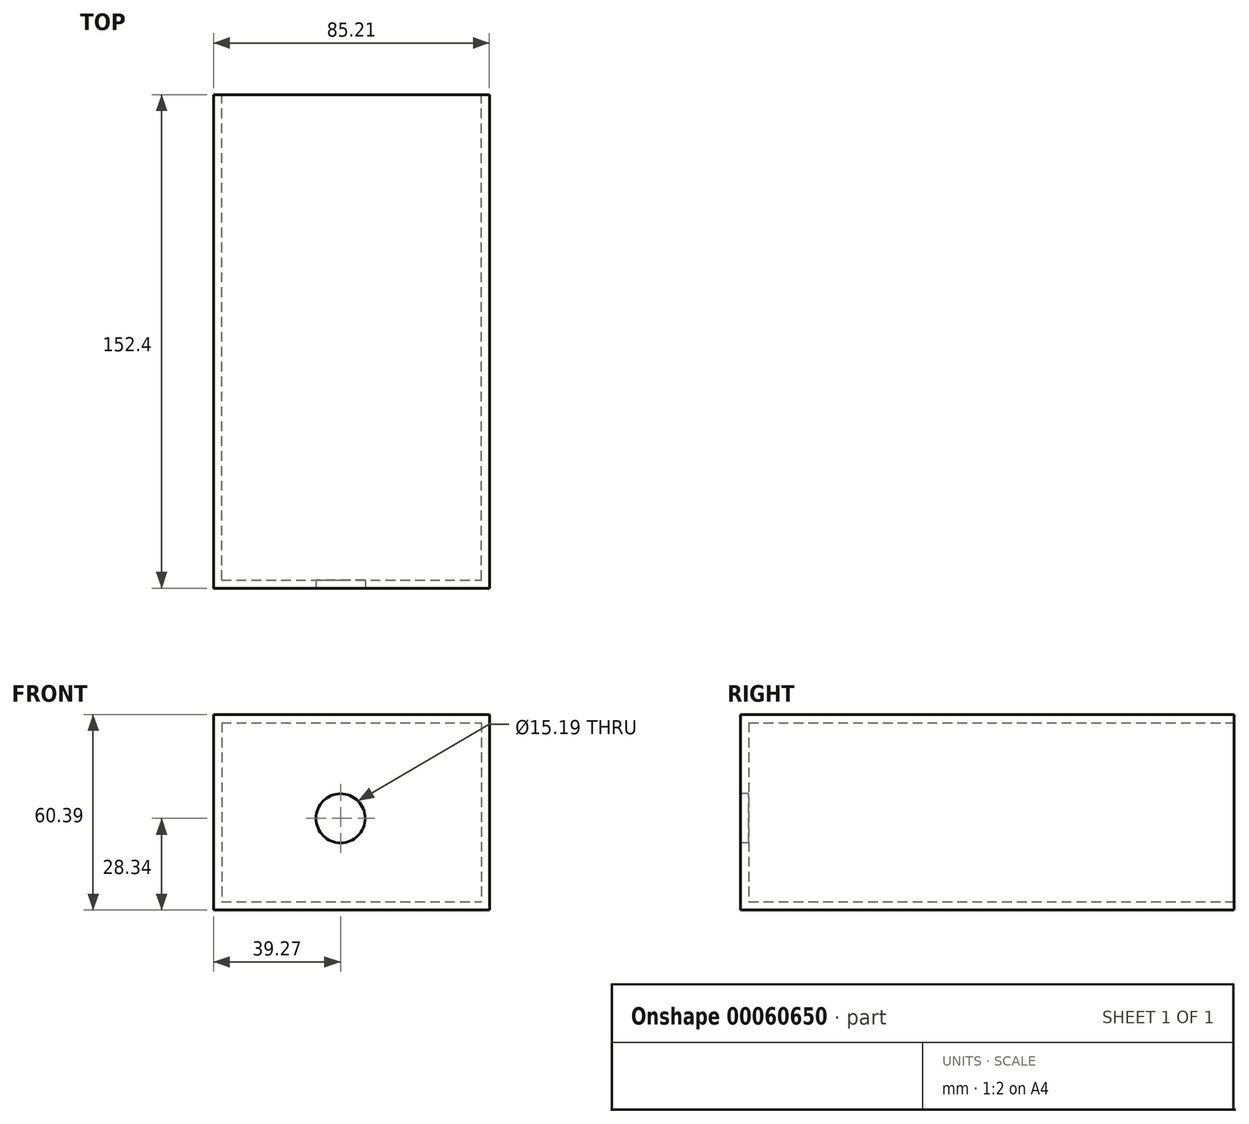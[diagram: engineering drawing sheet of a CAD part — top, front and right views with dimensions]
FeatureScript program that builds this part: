
annotation { "Feature Type Name" : "Feature", "Feature Type Description" : "" }
export const myFeature = defineFeature(function(context is Context, id is Id, definition is map)
    precondition{}
    {
        {
            var Q0;
            Q0=qCreatedBy(makeId("Front.planeOp"),FACE);
            var sketch = newSketch(context, id + "F0", { "sketchPlane" : qUnion([Q0])});
            skLineSegment(sketch, "E0.bottom", {"start": v(-39.27, 32.05) * mm, "end": v(45.94, 32.05) * mm});
            skLineSegment(sketch, "E0.top", {"start": v(-39.27, -28.34) * mm, "end": v(45.94, -28.34) * mm});
            skLineSegment(sketch, "E0.left", {"start": v(-39.27, 32.05) * mm, "end": v(-39.27, -28.34) * mm});
            skLineSegment(sketch, "E0.right", {"start": v(45.94, 32.05) * mm, "end": v(45.94, -28.34) * mm});
            skSolve(sketch);
        }
        {
            var Q0;
            Q0=makeQuery(id+"F0.imprint","IMPRINT",FACE,{"disambiguationData":[TD([[makeQuery(id+"F0.imprint","IMPRINT",EDGE,{"derivedFrom":sQuery(id+"F0.wireOp",EDGE,"E0.bottom")}),-1.0]])]});
            extrude(context, id + "F1", {"entities" : qUnion([Q0]), "depth" : 127 * mm});
        }
        {
            var Q0;
            Q0=makeQuery(id+"F1.opExtrude","CAP_FACE",FACE,{"disambiguationData":[OSD([sQuery(id+"F0.wireOp",EDGE,"E0.bottom"),sQuery(id+"F0.wireOp",EDGE,"E0.top"),sQuery(id+"F0.wireOp",EDGE,"E0.left"),sQuery(id+"F0.wireOp",EDGE,"E0.right")])],"isStart":true});
            var sketch = newSketch(context, id + "F2", { "sketchPlane" : qUnion([Q0])});
            skSolve(sketch);
        }
        {
            var Q0;
            Q0=makeQuery(id+"F2.imprint","IMPRINT",FACE,{"disambiguationData":[TD([[makeQuery(id+"F2.imprint","IMPRINT",EDGE,{"derivedFrom":makeQuery(id+"F1.opExtrude","CAP_EDGE",EDGE,{"disambiguationData":[OSD([sQuery(id+"F0.wireOp",EDGE,"E0.bottom")])],"isStart":true})}),1.0]])]});
            extrude(context, id + "F3", {"entities" : qUnion([Q0]), "operationType" : NewBodyOperationType.ADD, "depth" : 25.4 * mm});
        }
        {
            var Q0;
            Q0=makeQuery(id+"F3.opExtrude","CAP_FACE",FACE,{"disambiguationData":[OSD([sQuery(id+"F0.wireOp",EDGE,"E0.bottom"),sQuery(id+"F0.wireOp",EDGE,"E0.top"),sQuery(id+"F0.wireOp",EDGE,"E0.left"),sQuery(id+"F0.wireOp",EDGE,"E0.right")])],"isStart":false});
            shell(context, id + "F4", {"entities" : qUnion([Q0]), "thickness" : 2.54 * mm});
        }
        {
            var Q0;
            Q0=qCreatedBy(makeId("Front.planeOp"),FACE);
            var sketch = newSketch(context, id + "F5", { "sketchPlane" : qUnion([Q0])});
            skCircle(sketch, "E1", {"center": v(0, 0) * mm, "radius": 7.6 * mm});
            skSolve(sketch);
        }
        {
            var Q0;
            Q0 = qSketchRegion(id + "F5", true);
            extrude(context, id + "F6", {"entities" : qUnion([Q0]), "operationType" : NewBodyOperationType.REMOVE, "endBound" : BoundingType.SYMMETRIC, "oppositeDirection" : true, "depth" : 254 * mm});
        }
    });
